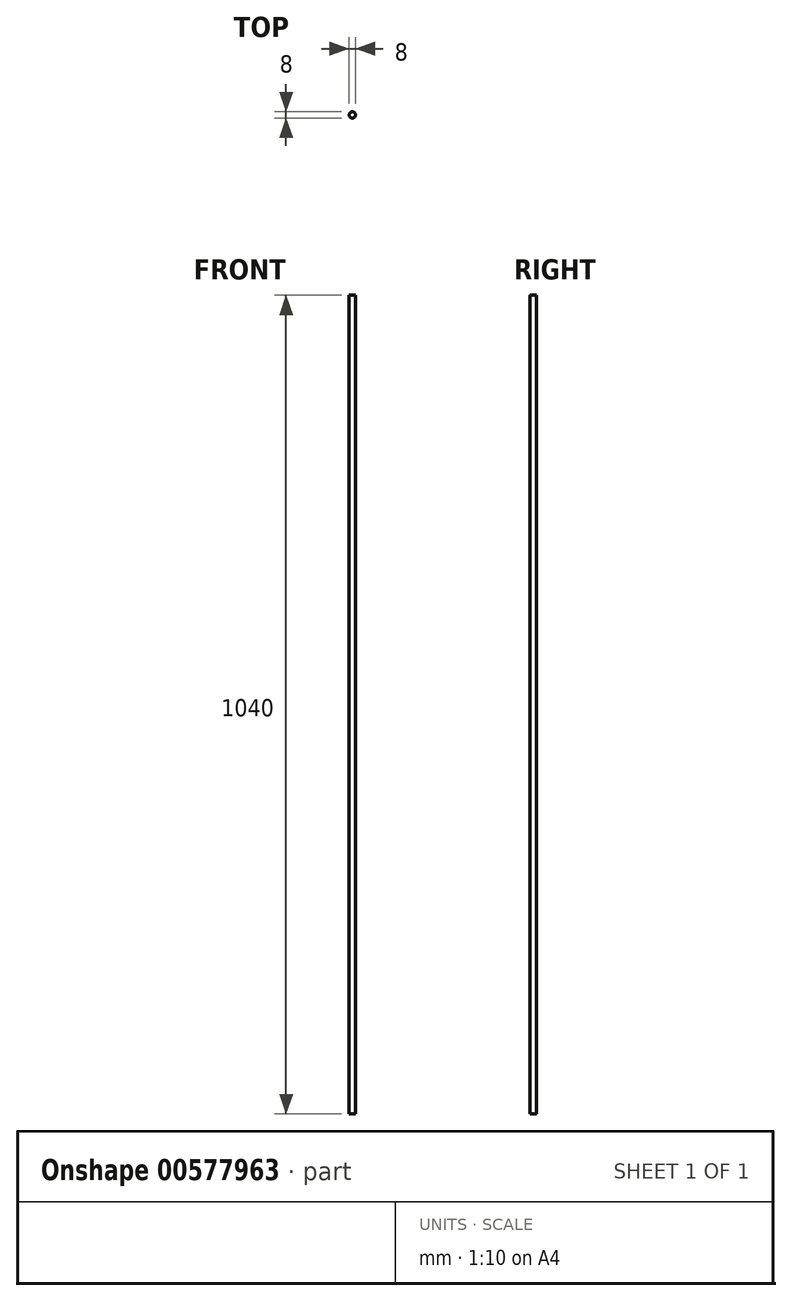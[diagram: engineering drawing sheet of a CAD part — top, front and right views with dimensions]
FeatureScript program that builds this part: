
annotation { "Feature Type Name" : "Feature", "Feature Type Description" : "" }
export const myFeature = defineFeature(function(context is Context, id is Id, definition is map)
    precondition{}
    {
        {
            var Q0;
            Q0=qCreatedBy(makeId("Top.planeOp"),FACE);
            var sketch = newSketch(context, id + "F0", { "sketchPlane" : qUnion([Q0])});
            skCircle(sketch, "E0", {"center": v(0, 0) * mm, "radius": 4 * mm});
            skSolve(sketch);
        }
        {
            var Q0;
            Q0=qSketchRegion(id+"F0",true);
            extrude(context, id + "F1", {"entities" : qUnion([Q0]), "depth" : 1040 * mm, "offsetDistance" : 25 * mm});
        }
    });
